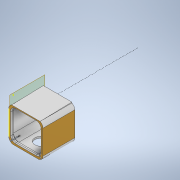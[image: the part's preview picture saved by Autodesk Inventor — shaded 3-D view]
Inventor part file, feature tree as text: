
AUTODESK INVENTOR PART (.ipt)
format: ipt  version: 2020 (Build 240168000, 168)  size: 297,984 bytes
history: native  units: in
note: dims shown in document units (in); Inventor stores cm internally (conversion verified against a paired STEP export)
features: sketch x7, extrude x6, projected_geometry x5, other x3, fillet x2, plane x1
ambient origin geometry x8: Origin, YZ Plane, XZ Plane, XY Plane, X Axis, Y Axis, Z Axis, Center Point
bodies: Solid1 (feature_tree)
feature tree (24):
  other  "Assembly4.iam"
  other  "Kauri modular session 5 mount.ipt:1"
  other  "session 5.ipt:1"
  extrude  "Extrusion1"  Depth=0.3937in TaperAngle=0.0deg
  extrude  "Extrusion2"  Depth=1.0in TaperAngle=0.0deg
  extrude  "Extrusion3"  Depth=0.3937in TaperAngle=0.0deg
  fillet  "Fillet1"  Radius=0.2362in
  fillet  "Fillet2"  Radius=0.0394in
  extrude  "Extrusion4"  Depth=0.3937in
  extrude  "Extrusion5"  Depth=0.0197in
  sketch  "Sketch6"  dims[d20=0.0197in d21=0.3937in d22=0.0in]
  plane  "Work Plane1"
  extrude  "Extrusion6"  Depth=0.3937in TaperAngle=0.0deg
  sketch  "Sketch1"  dims[d0=0.3937in d1=1.0in d2=0.0in]
  projected_geometry  "Projected Loop1"
  sketch  "Sketch2"  dims[d3=0.5906in d4=1.0in d5=0.0in]
  sketch  "Sketch3"  dims[d6=0.9843in d7=0.3937in d8=0.0in d9=0.2362in d10=0.0394in]
  projected_geometry  "Projected Loop2"
  sketch  "Sketch4"  dims[d12=0.0197in d15=0.3937in d16=0.0in d17=0.0197in]
  projected_geometry  "Projected Loop3"
  sketch  "Sketch5"  dims[d18=0.0197in d19=0.0197in]
  projected_geometry  "Projected Loop4"
  projected_geometry  "Projected Loop5"
  sketch  "Sketch7"  dims[d23=0.0in d24=0.0394in d25=1.378in d26=0.0in]
